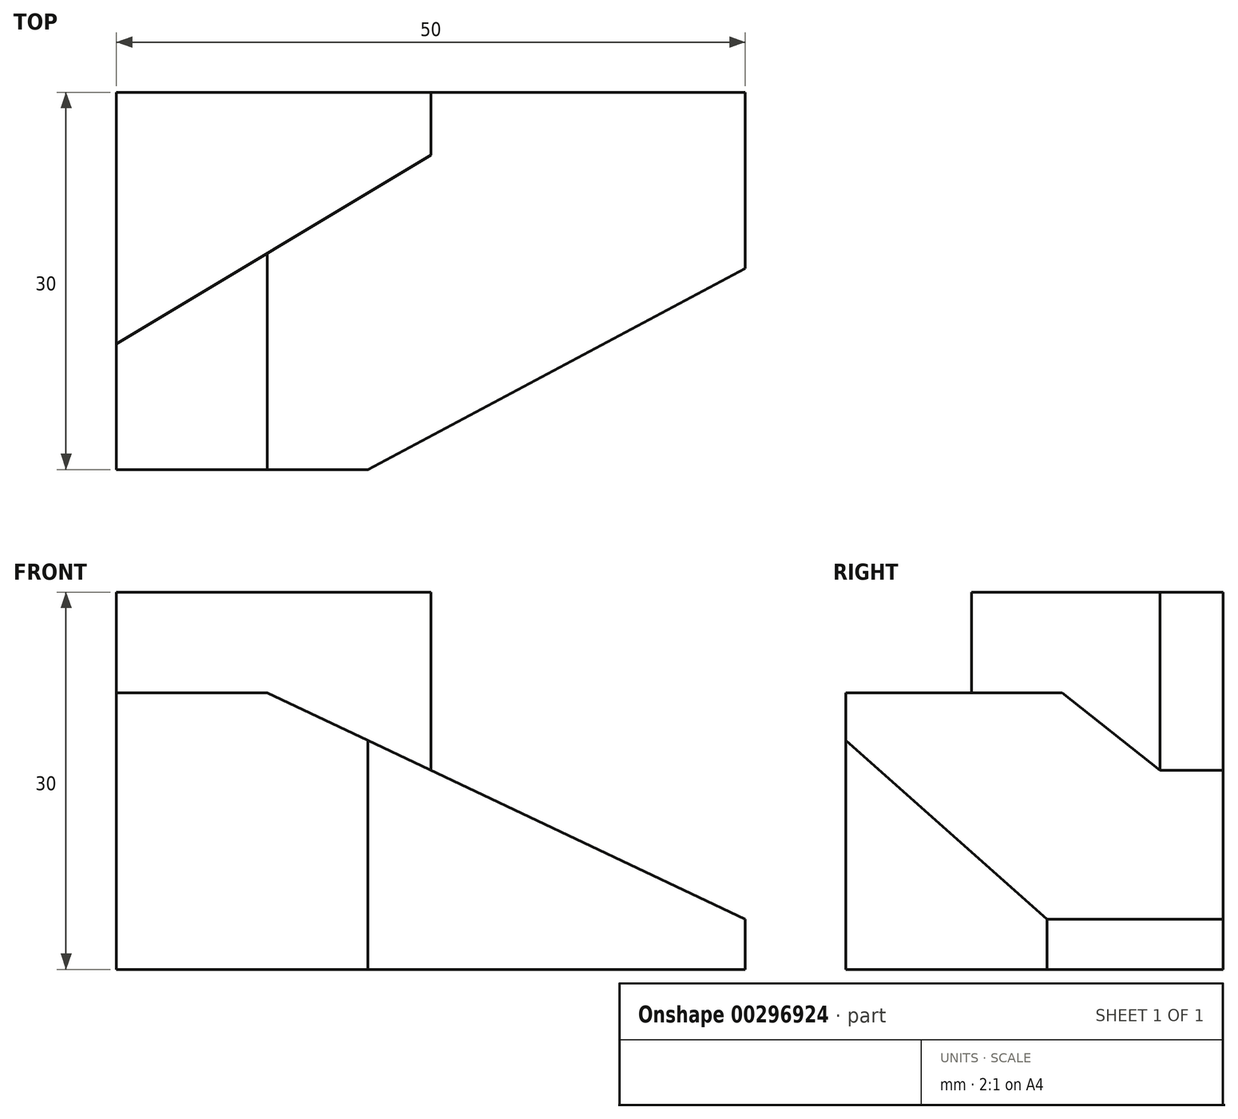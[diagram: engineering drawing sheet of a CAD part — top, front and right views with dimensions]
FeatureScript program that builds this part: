
annotation { "Feature Type Name" : "Feature", "Feature Type Description" : "" }
export const myFeature = defineFeature(function(context is Context, id is Id, definition is map)
    precondition{}
    {
        {
            var Q0;
            Q0=qCreatedBy(makeId("Front.planeOp"),FACE);
            var sketch = newSketch(context, id + "F0", { "sketchPlane" : qUnion([Q0])});
            skLineSegment(sketch, "E0.bottom", {"start": v(0, 0) * mm, "end": v(50, 0) * mm});
            skLineSegment(sketch, "E0.top", {"start": v(0, 22) * mm, "end": v(50, 22) * mm});
            skLineSegment(sketch, "E0.left", {"start": v(0, 0) * mm, "end": v(0, 22) * mm});
            skLineSegment(sketch, "E0.right", {"start": v(50, 0) * mm, "end": v(50, 22) * mm});
            skLineSegment(sketch, "E1", {"start": v(12, 22) * mm, "end": v(50, 4) * mm});
            skSolve(sketch);
        }
        {
            var Q0;
            {var subQ1=sQuery(id+"F0.wireOp",EDGE,"E0.bottom");Q0=makeQuery(id+"F0.imprint","IMPRINT",FACE,{"disambiguationData":[TD([[makeQuery(id+"F0.imprint","IMPRINT",EDGE,{"derivedFrom":subQ1}),1.0]])]});}
            extrude(context, id + "F1", {"entities" : qUnion([Q0]), "oppositeDirection" : true, "depth" : 30 * mm});
        }
        {
            var Q0;
            Q0=makeQuery(id+"F1.opExtrude","SWEPT_FACE",FACE,{"disambiguationData":[OSD([sQuery(id+"F0.wireOp",EDGE,"E0.bottom")])]});
            var sketch = newSketch(context, id + "F2", { "sketchPlane" : qUnion([Q0])});
            skLineSegment(sketch, "E2", {"start": v(25, -30) * mm, "end": v(25, -25) * mm});
            skLineSegment(sketch, "E3", {"start": v(25, -25) * mm, "end": v(0, -10) * mm});
            skLineSegment(sketch, "E4", {"start": v(50, -16) * mm, "end": v(20, 0) * mm});
            skSolve(sketch);
        }
        {
            var Q0;
            {var subQ0=sQuery(id+"F2.wireOp",EDGE,"E4");Q0=makeQuery(id+"F2.imprint","IMPRINT",FACE,{"disambiguationData":[TD([[makeQuery(id+"F2.imprint","IMPRINT",EDGE,{"derivedFrom":subQ0}),-1.0]])]});}
            extrude(context, id + "F3", {"entities" : qUnion([Q0]), "operationType" : NewBodyOperationType.REMOVE, "endBound" : BoundingType.THROUGH_ALL, "oppositeDirection" : true, "depth" : 25 * mm});
        }
        {
            var Q0;
            {var subQ0=sQuery(id+"F2.wireOp",EDGE,"E2");Q0=makeQuery(id+"F2.imprint","IMPRINT",FACE,{"disambiguationData":[TD([[makeQuery(id+"F2.imprint","IMPRINT",EDGE,{"derivedFrom":subQ0}),1.0]])]});}
            extrude(context, id + "F4", {"entities" : qUnion([Q0]), "operationType" : NewBodyOperationType.ADD, "oppositeDirection" : true, "depth" : 30 * mm});
        }
    });
